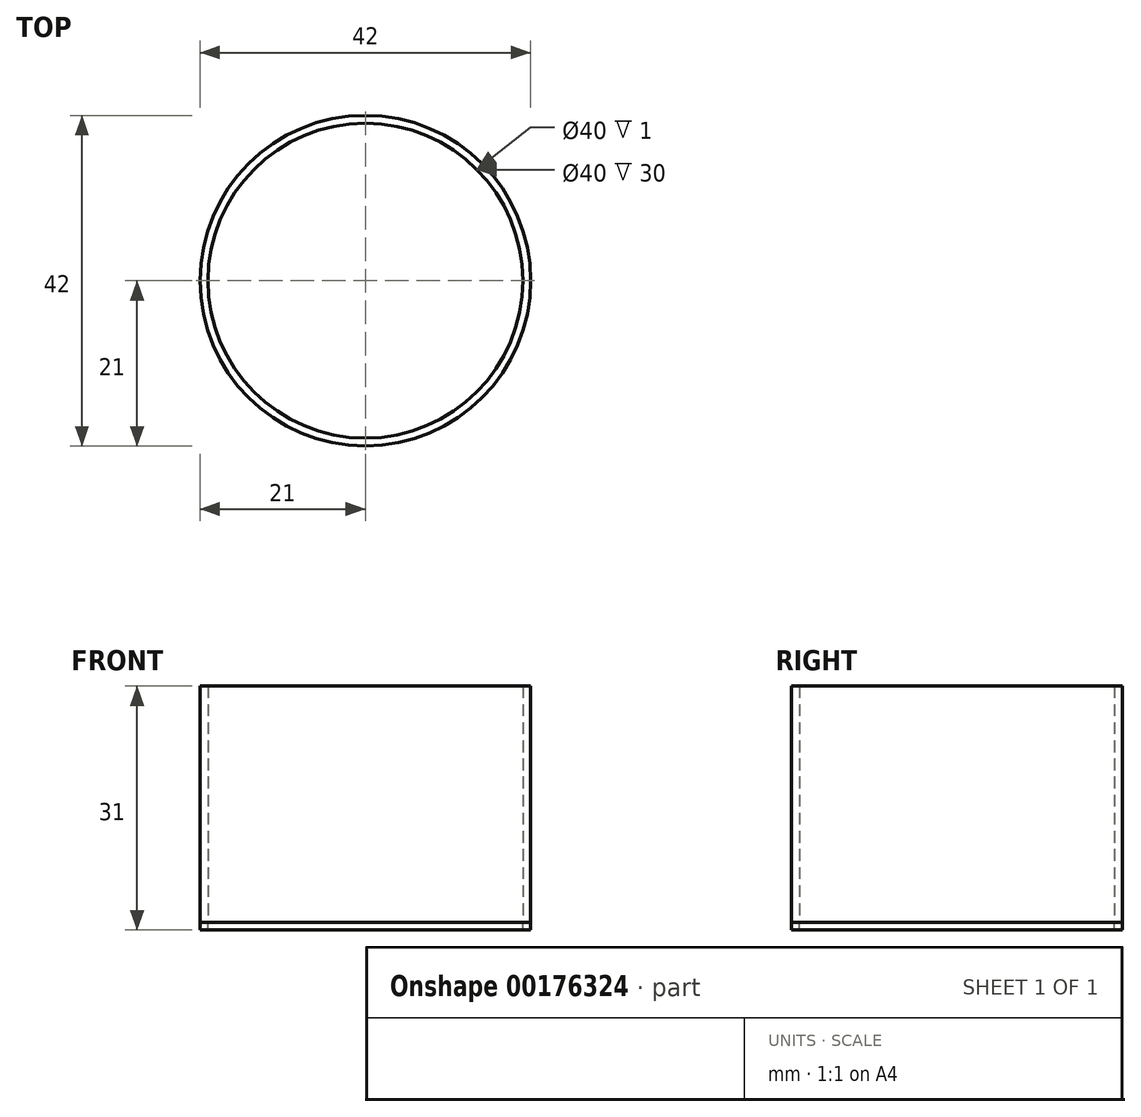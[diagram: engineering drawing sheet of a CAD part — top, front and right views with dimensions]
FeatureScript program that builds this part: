
annotation { "Feature Type Name" : "Feature", "Feature Type Description" : "" }
export const myFeature = defineFeature(function(context is Context, id is Id, definition is map)
    precondition{}
    {
        {
            var Q0;
            Q0=qCreatedBy(makeId("Top.planeOp"),FACE);
            var sketch = newSketch(context, id + "F0", { "sketchPlane" : qUnion([Q0])});
            skCircle(sketch, "E0", {"center": v(0, 0) * mm, "radius": 20 * mm});
            skCircle(sketch, "E1.0", {"center": v(0, 0) * mm, "radius": 21 * mm});
            skSolve(sketch);
        }
        {
            var Q0;
            Q0=makeQuery(id+"F0.imprint","IMPRINT",FACE,{"disambiguationData":[TD([[makeQuery(id+"F0.imprint","IMPRINT",EDGE,{"derivedFrom":sQuery(id+"F0.wireOp",EDGE,"E0")}),-1.0]])]});
            extrude(context, id + "F1", {"entities" : qUnion([Q0]), "depth" : 30 * mm});
        }
        {
            var Q0;
            Q0=makeQuery(id+"F0.imprint","IMPRINT",FACE,{"disambiguationData":[TD([[makeQuery(id+"F0.imprint","IMPRINT",EDGE,{"derivedFrom":sQuery(id+"F0.wireOp",EDGE,"E0")}),1.0]])]});
            extrude(context, id + "F2", {"entities" : qUnion([Q0]), "oppositeDirection" : true, "depth" : 1 * mm});
        }
        {
            var Q0;
            Q0=makeQuery(id+"F1.opExtrude","CAP_FACE",FACE,{"disambiguationData":[OSD([sQuery(id+"F0.wireOp",EDGE,"E0"),sQuery(id+"F0.wireOp",EDGE,"E1.0")])],"isStart":true});
            extrude(context, id + "F3", {"entities" : qUnion([Q0]), "depth" : 1 * mm});
        }
    });
